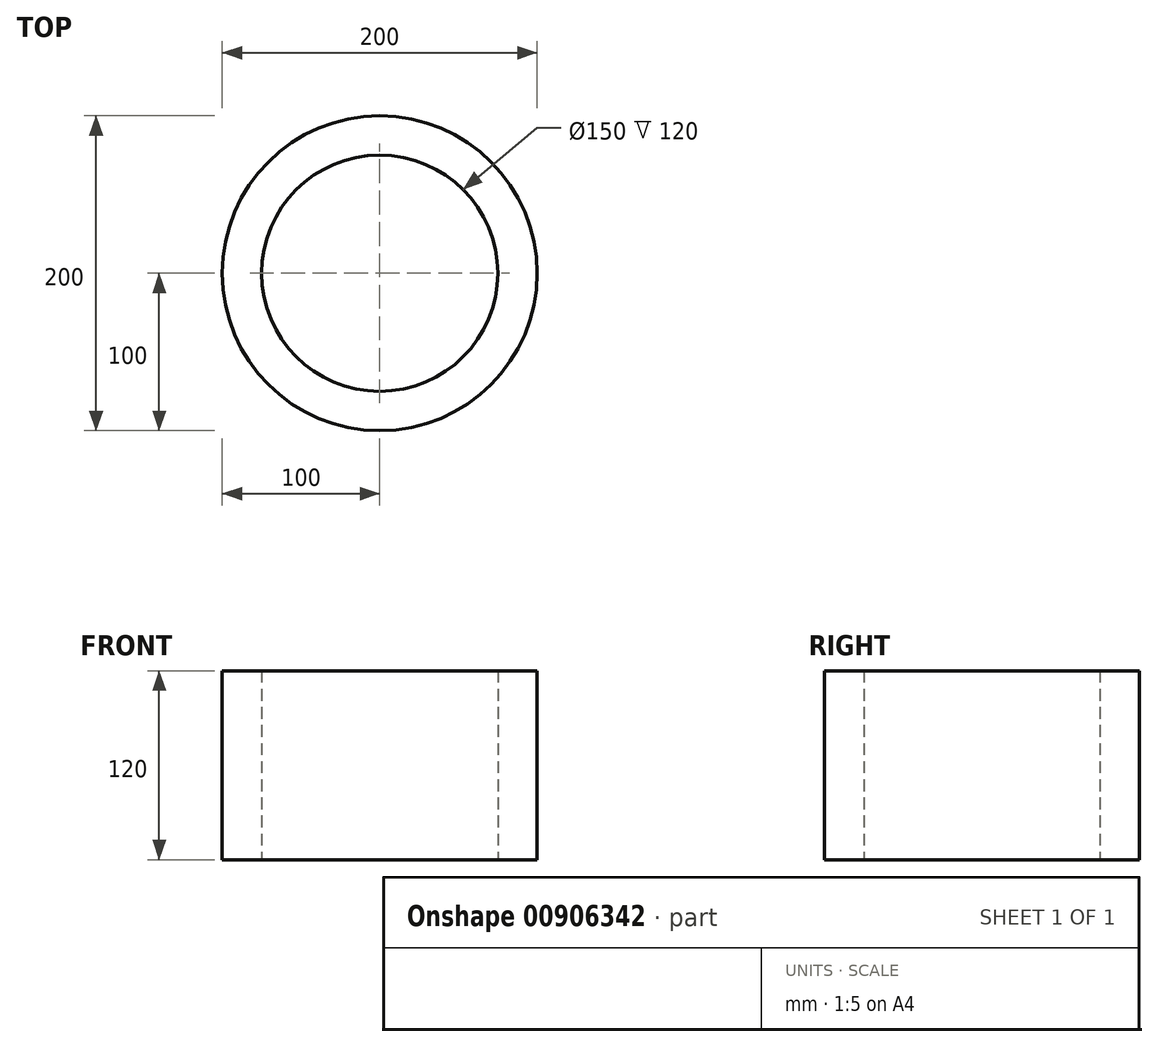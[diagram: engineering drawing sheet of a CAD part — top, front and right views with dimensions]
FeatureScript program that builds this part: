
annotation { "Feature Type Name" : "Feature", "Feature Type Description" : "" }
export const myFeature = defineFeature(function(context is Context, id is Id, definition is map)
    precondition{}
    {
        {
            var Q0;
            Q0=qCreatedBy(makeId("Top.planeOp"),FACE);
            var sketch = newSketch(context, id + "F0", { "sketchPlane" : qUnion([Q0])});
            skCircle(sketch, "E0", {"center": v(0, 0) * mm, "radius": 100 * mm});
            skCircle(sketch, "E1", {"center": v(0, 0) * mm, "radius": 75 * mm});
            skSolve(sketch);
        }
        {
            var Q0;
            Q0=makeQuery(id+"F0.imprint","IMPRINT",FACE,{"disambiguationData":[TD([[makeQuery(id+"F0.imprint","IMPRINT",EDGE,{"derivedFrom":sQuery(id+"F0.wireOp",EDGE,"E0")}),1.0]])]});
            extrude(context, id + "F1", {"entities" : qUnion([Q0]), "depth" : 120 * mm, "offsetDistance" : 25 * mm});
        }
    });
